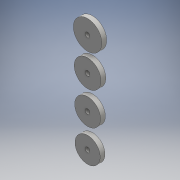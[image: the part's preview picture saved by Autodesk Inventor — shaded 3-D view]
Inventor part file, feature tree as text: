
AUTODESK INVENTOR PART (.ipt)
format: ipt  version: 2016 (Build 200138000, 138)  size: 122,880 bytes
history: native  units: mm
features: extrude x1, sketch x1
ambient origin geometry x8: Origin, YZ Plane, XZ Plane, XY Plane, X Axis, Y Axis, Z Axis, Center Point
bodies: Solid1 (feature_tree)
feature tree (2):
  extrude  "Extrusion1"  Depth=3.195mm
  sketch  "Sketch1"  dims[d19=3.175mm d20=18.9mm d21=3.175mm d22=17.8mm d24=3.175mm d25=17.14mm d27=3.175mm d28=16.7mm d30=22.0mm d31=22.0mm d32=22.0mm d33=3.195mm d34=0.0mm]
